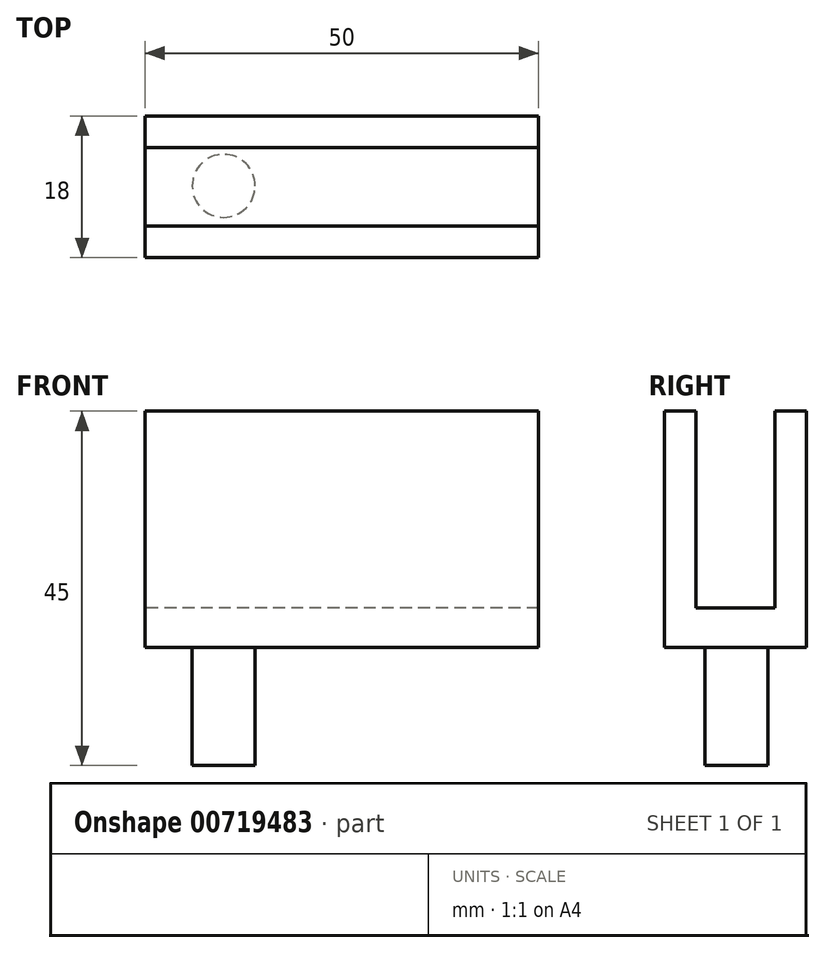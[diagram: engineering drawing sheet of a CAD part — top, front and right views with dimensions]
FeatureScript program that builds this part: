
annotation { "Feature Type Name" : "Feature", "Feature Type Description" : "" }
export const myFeature = defineFeature(function(context is Context, id is Id, definition is map)
    precondition{}
    {
        {
            var Q0;
            Q0=qCreatedBy(makeId("Top.planeOp"),FACE);
            var sketch = newSketch(context, id + "F0", { "sketchPlane" : qUnion([Q0])});
            skCircle(sketch, "E0", {"center": v(0, 0.14) * mm, "radius": 4 * mm});
            skSolve(sketch);
        }
        {
            var Q0;
            Q0=makeQuery(id+"F0.imprint","IMPRINT",FACE,{"disambiguationData":[TD([[makeQuery(id+"F0.imprint","IMPRINT",EDGE,{"derivedFrom":sQuery(id+"F0.wireOp",EDGE,"E0")}),1.0]])]});
            extrude(context, id + "F1", {"entities" : qUnion([Q0]), "depth" : 15 * mm, "offsetDistance" : 25 * mm});
        }
        {
            var Q0;
            Q0=makeQuery(id+"F1.opExtrude","CAP_FACE",FACE,{"disambiguationData":[OSD([sQuery(id+"F0.wireOp",EDGE,"E0")])],"isStart":false});
            var sketch = newSketch(context, id + "F2", { "sketchPlane" : qUnion([Q0])});
            skLineSegment(sketch, "E1.bottom", {"start": v(-10, 9) * mm, "end": v(40, 9) * mm});
            skLineSegment(sketch, "E1.top", {"start": v(-10, -9) * mm, "end": v(40, -9) * mm});
            skLineSegment(sketch, "E1.left", {"start": v(-10, 9) * mm, "end": v(-10, -9) * mm});
            skLineSegment(sketch, "E1.right", {"start": v(40, 9) * mm, "end": v(40, -9) * mm});
            skLineSegment(sketch, "E2", {"start": v(0, 0) * mm, "end": v(40, 0) * mm, "construction": true});
            skLineSegment(sketch, "E3", {"start": v(0, 0) * mm, "end": v(0, -9) * mm, "construction": true});
            skSolve(sketch);
        }
        {
            var Q0;
            Q0=makeQuery(id+"F2.imprint","IMPRINT",FACE,{"disambiguationData":[TD([[makeQuery(id+"F2.imprint","IMPRINT",EDGE,{"derivedFrom":sQuery(id+"F2.wireOp",EDGE,"E1.bottom")}),-1.0]])]});
            var Q1;
            Q1=makeQuery(id+"F2.imprint","IMPRINT",FACE,{"disambiguationData":[TD([[makeQuery(id+"F2.imprint","IMPRINT",EDGE,{"derivedFrom":makeQuery(id+"F1.opExtrude","CAP_EDGE",EDGE,{"disambiguationData":[OSD([sQuery(id+"F0.wireOp",EDGE,"E0")])],"isStart":false})}),1.0]])]});
            extrude(context, id + "F3", {"entities" : qUnion([Q0, Q1]), "operationType" : NewBodyOperationType.ADD, "depth" : 30 * mm, "offsetDistance" : 25 * mm});
        }
        {
            var Q0;
            Q0=qCreatedBy(makeId("Front.planeOp"),FACE);
            var sketch = newSketch(context, id + "F4", { "sketchPlane" : qUnion([Q0])});
            skLineSegment(sketch, "E4.bottom", {"start": v(40, 45) * mm, "end": v(-10, 45) * mm});
            skLineSegment(sketch, "E4.top", {"start": v(40, 20) * mm, "end": v(-10, 20) * mm});
            skLineSegment(sketch, "E4.left", {"start": v(40, 45) * mm, "end": v(40, 20) * mm});
            skLineSegment(sketch, "E4.right", {"start": v(-10, 45) * mm, "end": v(-10, 20) * mm});
            skSolve(sketch);
        }
        {
            var Q0;
            Q0 = qSketchRegion(id + "F4", true);
            extrude(context, id + "F5", {"entities" : qUnion([Q0]), "operationType" : NewBodyOperationType.REMOVE, "endBound" : BoundingType.SYMMETRIC, "oppositeDirection" : true, "depth" : 10 * mm, "offsetDistance" : 25 * mm});
        }
    });
